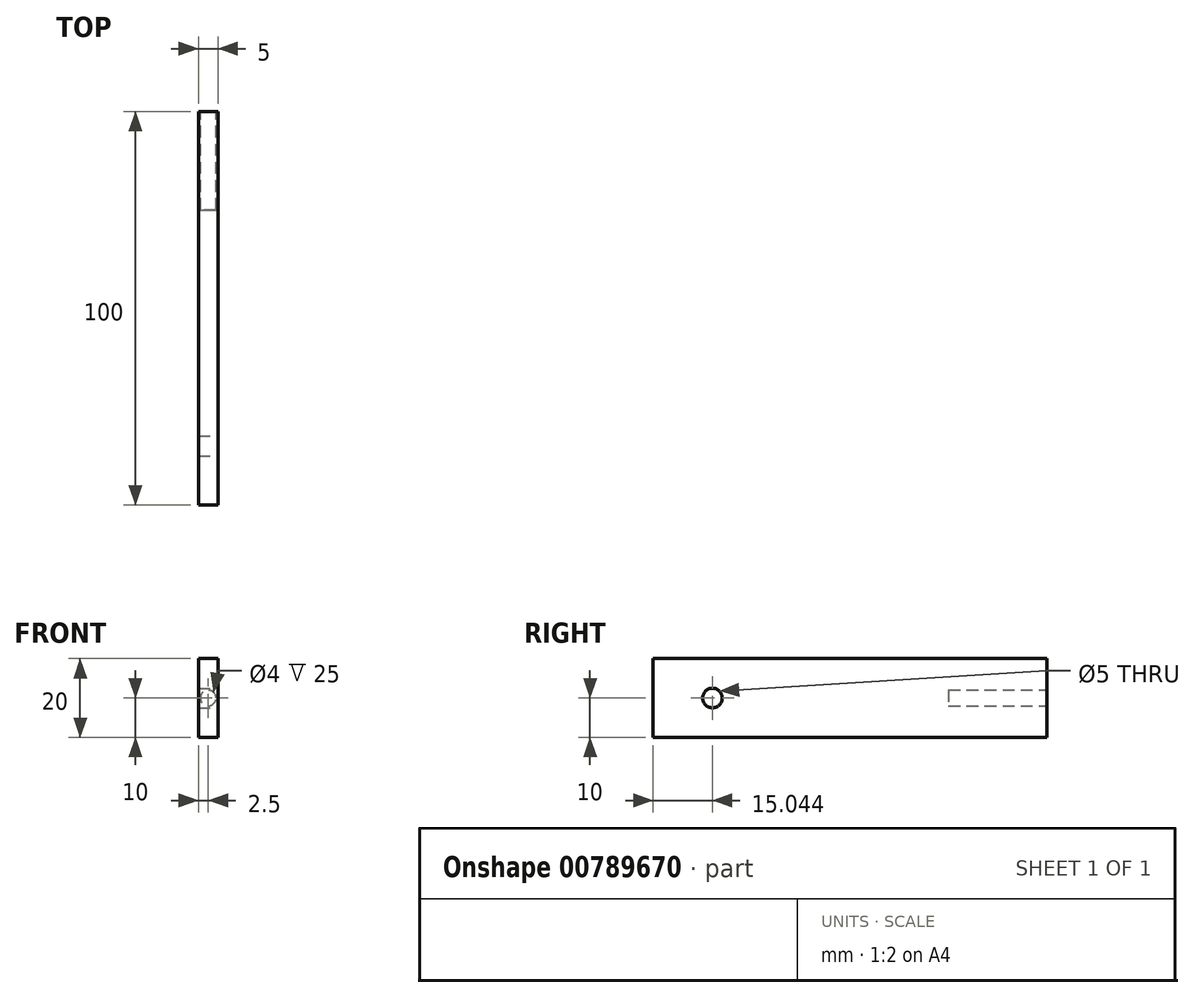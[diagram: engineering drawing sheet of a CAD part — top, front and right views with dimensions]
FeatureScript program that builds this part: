
annotation { "Feature Type Name" : "Feature", "Feature Type Description" : "" }
export const myFeature = defineFeature(function(context is Context, id is Id, definition is map)
    precondition{}
    {
        {
            var Q0;
            Q0=qCreatedBy(makeId("Front.planeOp"),FACE);
            var sketch = newSketch(context, id + "F0", { "sketchPlane" : qUnion([Q0])});
            skLineSegment(sketch, "E0.bottom", {"start": v(0, 0) * mm, "end": v(5, 0) * mm});
            skLineSegment(sketch, "E0.top", {"start": v(0, -20) * mm, "end": v(5, -20) * mm});
            skLineSegment(sketch, "E0.left", {"start": v(0, 0) * mm, "end": v(0, -20) * mm});
            skLineSegment(sketch, "E0.right", {"start": v(5, 0) * mm, "end": v(5, -20) * mm});
            skSolve(sketch);
        }
        {
            var Q0;
            Q0 = qSketchRegion(id + "F0", true);
            extrude(context, id + "F1", {"entities" : qUnion([Q0]), "depth" : 100 * mm, "offsetDistance" : 25 * mm});
        }
        {
            var Q0;
            Q0=makeQuery(id+"F1.opExtrude","CAP_FACE",FACE,{"disambiguationData":[OSD([sQuery(id+"F0.wireOp",EDGE,"E0.bottom"),sQuery(id+"F0.wireOp",EDGE,"E0.top"),sQuery(id+"F0.wireOp",EDGE,"E0.left"),sQuery(id+"F0.wireOp",EDGE,"E0.right")])],"isStart":true});
            var sketch = newSketch(context, id + "F2", { "sketchPlane" : qUnion([Q0])});
            skCircle(sketch, "E1", {"center": v(-2.5, -10) * mm, "radius": 2 * mm});
            skPoint(sketch, "E1.centerSnap0", {"position": v(-5, -10) * mm});
            skPoint(sketch, "E1.centerSnap1", {"position": v(-2.5, -20) * mm});
            skSolve(sketch);
        }
        {
            var Q0;
            Q0=makeQuery(id+"F2.imprint","IMPRINT",FACE,{"disambiguationData":[TD([[makeQuery(id+"F2.imprint","IMPRINT",EDGE,{"derivedFrom":sQuery(id+"F2.wireOp",EDGE,"E1")}),1.0]])]});
            extrude(context, id + "F3", {"entities" : qUnion([Q0]), "operationType" : NewBodyOperationType.REMOVE, "oppositeDirection" : true, "depth" : 25 * mm, "offsetDistance" : 25 * mm});
        }
        {
            var Q0;
            Q0=makeQuery(id+"F1.opExtrude","SWEPT_FACE",FACE,{"disambiguationData":[OSD([sQuery(id+"F0.wireOp",EDGE,"E0.right")])]});
            var sketch = newSketch(context, id + "F4", { "sketchPlane" : qUnion([Q0])});
            skCircle(sketch, "E2", {"center": v(-84.96, -10) * mm, "radius": 2.5 * mm});
            skPoint(sketch, "E2.centerSnap0", {"position": v(-100, -10) * mm});
            skSolve(sketch);
        }
        {
            var Q0;
            Q0 = qSketchRegion(id + "F4", true);
            extrude(context, id + "F5", {"entities" : qUnion([Q0]), "operationType" : NewBodyOperationType.REMOVE, "endBound" : BoundingType.THROUGH_ALL, "oppositeDirection" : true, "depth" : 25 * mm, "offsetDistance" : 25 * mm});
        }
    });
